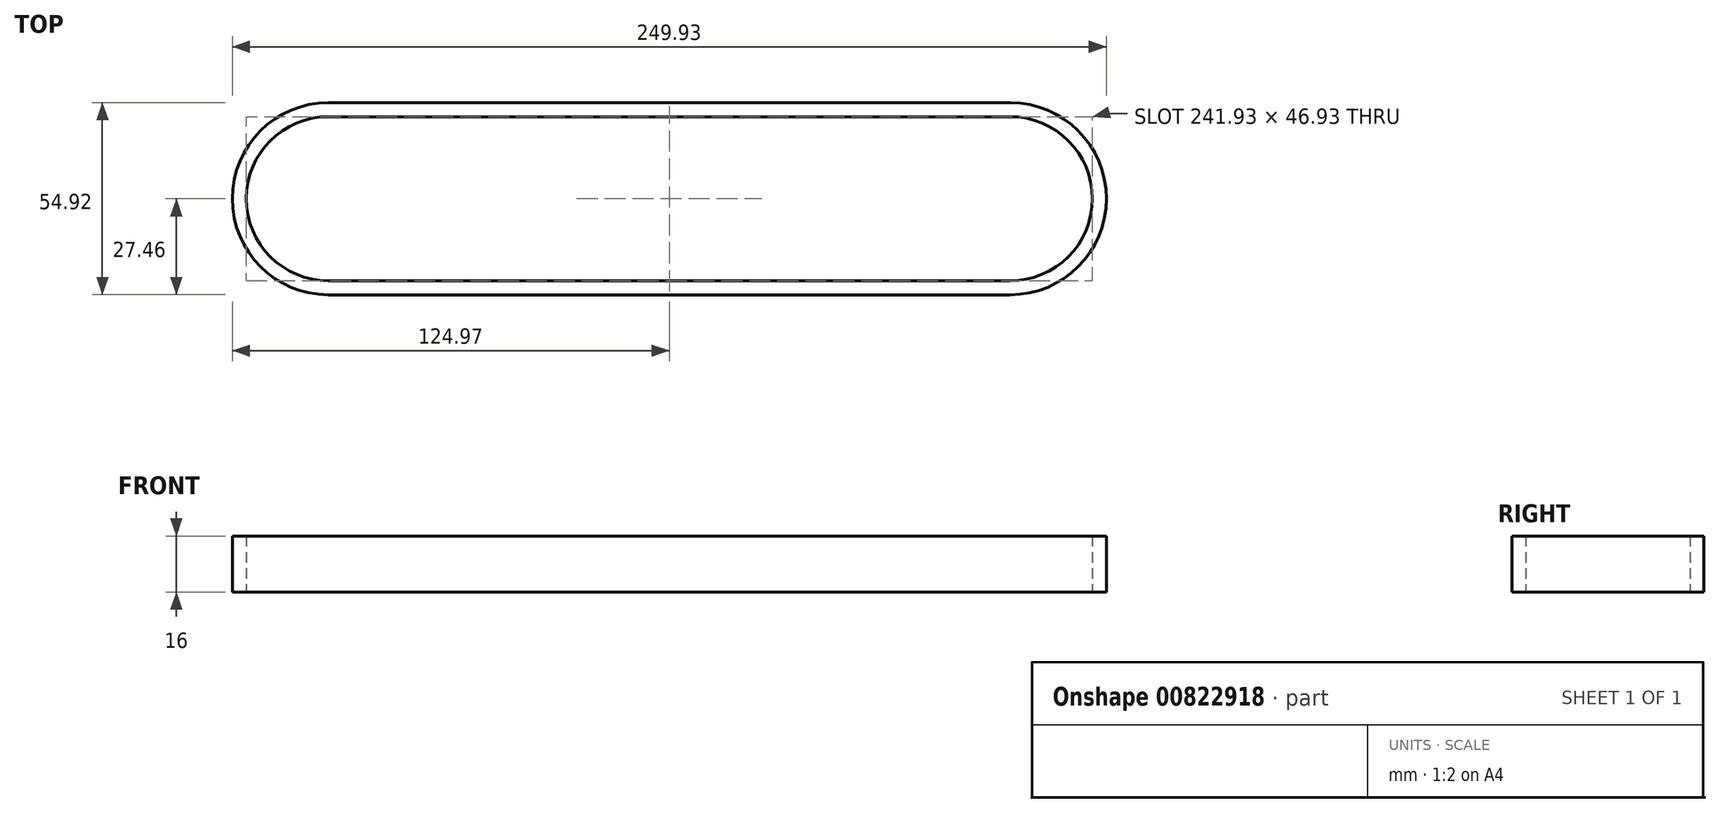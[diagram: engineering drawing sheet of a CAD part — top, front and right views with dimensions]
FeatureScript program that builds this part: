
annotation { "Feature Type Name" : "Feature", "Feature Type Description" : "" }
export const myFeature = defineFeature(function(context is Context, id is Id, definition is map)
    precondition{}
    {
        {
            var Q0;
            Q0=qCreatedBy(makeId("Top.planeOp"),FACE);
            var sketch = newSketch(context, id + "F0", { "sketchPlane" : qUnion([Q0])});
            skArc(sketch, "E0", {"start": v(0, -25.46) * mm, "mid": v(25.46, 0) * mm, "end": v(0, 25.46) * mm, "construction": true});
            skLineSegment(sketch, "E1", {"start": v(0, 0) * mm, "end": v(-195, 0) * mm, "construction": true});
            skArc(sketch, "E2", {"start": v(-195, 25.46) * mm, "mid": v(-220.47, 0) * mm, "end": v(-195, -25.47) * mm, "construction": true});
            skLineSegment(sketch, "E3", {"start": v(0, 0) * mm, "end": v(0, 25.46) * mm, "construction": true});
            skLineSegment(sketch, "E4", {"start": v(0, 0) * mm, "end": v(0, -25.46) * mm, "construction": true});
            skLineSegment(sketch, "E5", {"start": v(-195, 0) * mm, "end": v(-195, 25.47) * mm, "construction": true});
            skLineSegment(sketch, "E6", {"start": v(-195, 0) * mm, "end": v(-195, -25.47) * mm, "construction": true});
            skLineSegment(sketch, "E7", {"start": v(-195, 25.46) * mm, "end": v(0, 25.47) * mm, "construction": true});
            skLineSegment(sketch, "E8", {"start": v(-195, -25.47) * mm, "end": v(0, -25.47) * mm, "construction": true});
            skArc(sketch, "E9.0", {"start": v(-195, 23.46) * mm, "mid": v(-218.47, 0) * mm, "end": v(-195, -23.47) * mm});
            skLineSegment(sketch, "E10.0", {"start": v(-195, 23.47) * mm, "end": v(0, 23.47) * mm});
            skLineSegment(sketch, "E11.0", {"start": v(-195, -27.47) * mm, "end": v(0, -27.47) * mm});
            skArc(sketch, "E12.0", {"start": v(-195, 27.46) * mm, "mid": v(-222.47, 0) * mm, "end": v(-195, -27.47) * mm});
            skLineSegment(sketch, "E13.0", {"start": v(-195, 27.47) * mm, "end": v(0, 27.46) * mm});
            skArc(sketch, "E14.0", {"start": v(0, -27.47) * mm, "mid": v(27.47, 0) * mm, "end": v(0, 27.47) * mm});
            skArc(sketch, "E15.0", {"start": v(0, -23.46) * mm, "mid": v(23.46, 0) * mm, "end": v(0, 23.46) * mm});
            skLineSegment(sketch, "E16.0", {"start": v(-195, -23.47) * mm, "end": v(0, -23.47) * mm});
            skSolve(sketch);
        }
        {
            var Q0;
            Q0=qSketchRegion(id+"F0",true);
            extrude(context, id + "F1", {"entities" : qUnion([Q0]), "endBound" : BoundingType.SYMMETRIC, "depth" : 16 * mm, "offsetDistance" : 25 * mm});
        }
    });
